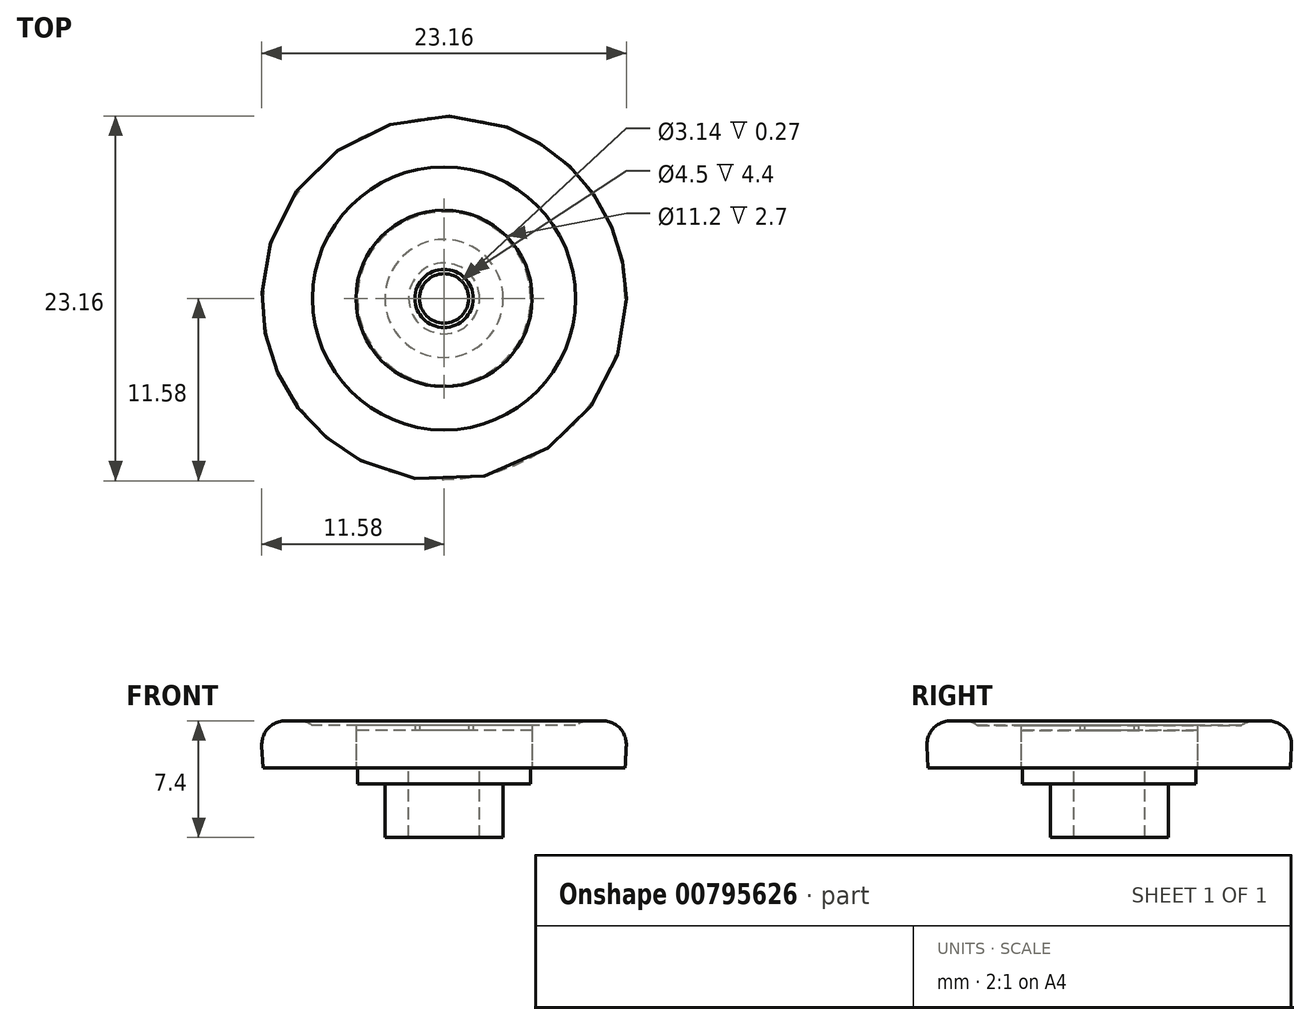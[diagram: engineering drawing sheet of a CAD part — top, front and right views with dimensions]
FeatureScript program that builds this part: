
annotation { "Feature Type Name" : "Feature", "Feature Type Description" : "" }
export const myFeature = defineFeature(function(context is Context, id is Id, definition is map)
    precondition{}
    {
        {
            var Q0;
            Q0=qCreatedBy(makeId("Top.planeOp"),FACE);
            var sketch = newSketch(context, id + "F0", { "sketchPlane" : qUnion([Q0])});
            skCircle(sketch, "E0", {"center": v(0, 0) * mm, "radius": 11.5 * mm});
            skCircle(sketch, "E1", {"center": v(0, 0) * mm, "radius": 8.5 * mm});
            skCircle(sketch, "E2", {"center": v(0, 0) * mm, "radius": 5.6 * mm});
            skSolve(sketch);
        }
        {
            var Q0;
            Q0 = qSketchRegion(id + "F0", true);
            extrude(context, id + "F1", {"entities" : qUnion([Q0]), "depth" : 3 * mm, "offsetDistance" : 25 * mm, "hasDraft" : true, "draftAngle" : 3 * degree});
        }
        {
            var Q0;
            Q0=makeQuery(id+"F0.imprint","IMPRINT",FACE,{"disambiguationData":[TD([[makeQuery(id+"F0.imprint","IMPRINT",EDGE,{"derivedFrom":sQuery(id+"F0.wireOp",EDGE,"E1")}),1.0]])]});
            extrude(context, id + "F2", {"entities" : qUnion([Q0]), "operationType" : NewBodyOperationType.ADD, "depth" : 2.7 * mm, "offsetDistance" : 25 * mm});
        }
        {
            var Q0;
            Q0=makeQuery(id+"F0.imprint","IMPRINT",FACE,{"disambiguationData":[TD([[makeQuery(id+"F0.imprint","IMPRINT",EDGE,{"derivedFrom":sQuery(id+"F0.wireOp",EDGE,"sJWBEL4Q-zqKP-wKAH-Xvia-YZl9IQGTlxIB")}),1.0]])]});
            var Q1;
            Q1=makeQuery(id+"F0.imprint","IMPRINT",FACE,{"disambiguationData":[TD([[makeQuery(id+"F0.imprint","IMPRINT",EDGE,{"derivedFrom":sQuery(id+"F0.wireOp",EDGE,"W3Ua214L-QGfU-jLto-IY45-T6SqmYm5Pf0N")}),1.0]])]});
            var Q2;
            Q2=makeQuery(id+"F0.imprint","IMPRINT",FACE,{"disambiguationData":[TD([[makeQuery(id+"F0.imprint","IMPRINT",EDGE,{"derivedFrom":sQuery(id+"F0.wireOp",EDGE,"KE1PqsyT-DHGX-8diU-NURI-yFHnlOPL5x9j")}),1.0]])]});
            var Q3;
            Q3=makeQuery(id+"F0.imprint","IMPRINT",FACE,{"disambiguationData":[TD([[makeQuery(id+"F0.imprint","IMPRINT",EDGE,{"derivedFrom":sQuery(id+"F0.wireOp",EDGE,"93cc1e78-3582-4651-860f-33596dd8aeea")}),1.0]])]});
            var Q4;
            Q4=makeQuery(id+"F0.imprint","IMPRINT",FACE,{"disambiguationData":[TD([[makeQuery(id+"F0.imprint","IMPRINT",EDGE,{"derivedFrom":sQuery(id+"F0.wireOp",EDGE,"580936a7-a73b-495c-908d-01e9c6adc14b")}),1.0]])]});
            var Q5;
            Q5=makeQuery(id+"F0.imprint","IMPRINT",FACE,{"disambiguationData":[TD([[makeQuery(id+"F0.imprint","IMPRINT",EDGE,{"derivedFrom":sQuery(id+"F0.wireOp",EDGE,"914aee80-40cc-4c9e-a0ba-7517bd072fba")}),1.0]])]});
            var Q6;
            Q6=makeQuery(id+"F0.imprint","IMPRINT",FACE,{"disambiguationData":[TD([[makeQuery(id+"F0.imprint","IMPRINT",EDGE,{"derivedFrom":sQuery(id+"F0.wireOp",EDGE,"tJGHLqfq-XDhS-PHHt-wrfx-KiIFVS5NVcas")}),1.0]])]});
            var Q7;
            Q7=makeQuery(id+"F0.imprint","IMPRINT",FACE,{"disambiguationData":[TD([[makeQuery(id+"F0.imprint","IMPRINT",EDGE,{"derivedFrom":sQuery(id+"F0.wireOp",EDGE,"QfYnkFk0-Tl5y-BypX-IXop-PRvAgd9sKDpf")}),1.0]])]});
            var Q8;
            Q8=makeQuery(id+"F0.imprint","IMPRINT",FACE,{"disambiguationData":[TD([[makeQuery(id+"F0.imprint","IMPRINT",EDGE,{"derivedFrom":sQuery(id+"F0.wireOp",EDGE,"Y070iHcx-JKvN-373v-bcgJ-Ptq9Z7jqXRuu")}),1.0]])]});
            var Q9;
            {var subQ0=sQuery(id+"F0.wireOp",EDGE,"364aceb5-e4ae-42a2-838b-8d2f1a538a20");var subQ5=sQuery(id+"F0.wireOp",EDGE,"E2");var subQ8=makeQuery(id+"F0.imprint","INTERSECT",VERTEX,{"disambiguationData":[OD(0.0)],"derivedFrom":[subQ5,subQ0]});Q9=makeQuery(id+"F0.imprint","IMPRINT",FACE,{"disambiguationData":[TD([[makeQuery(id+"F0.imprint","IMPRINT",EDGE,{"disambiguationData":[TD([[subQ8,1.0]])],"derivedFrom":subQ5}),1.0]])]});}
            var Q10;
            {var subQ1=sQuery(id+"F0.wireOp",EDGE,"E2");var subQ3=sQuery(id+"F0.wireOp",EDGE,"240fa6d0-75f4-4649-a5dc-fb8ea6b493ce");var subQ4=makeQuery(id+"F0.imprint","INTERSECT",VERTEX,{"disambiguationData":[OD(0.0)],"derivedFrom":[subQ1,subQ3]});Q10=makeQuery(id+"F0.imprint","IMPRINT",FACE,{"disambiguationData":[TD([[makeQuery(id+"F0.imprint","IMPRINT",EDGE,{"disambiguationData":[TD([[subQ4,-1.0]])],"derivedFrom":subQ1}),1.0]])]});}
            var Q11;
            {var subQ0=sQuery(id+"F0.wireOp",EDGE,"a4363b79-0781-4621-b503-21fbbac03dd4");Q11=makeQuery(id+"F0.imprint","IMPRINT",FACE,{"disambiguationData":[TD([[makeQuery(id+"F0.imprint","IMPRINT",EDGE,{"derivedFrom":subQ0}),1.0]])]});}
            var Q12;
            Q12=makeQuery(id+"F0.imprint","IMPRINT",FACE,{"disambiguationData":[TD([[makeQuery(id+"F0.imprint","IMPRINT",EDGE,{"derivedFrom":sQuery(id+"F0.wireOp",EDGE,"dakPGjOR-qgw5-qXTv-UFbR-eR2Q9f3JjfMY")}),1.0]])]});
            var Q13;
            Q13=makeQuery(id+"F0.imprint","IMPRINT",FACE,{"disambiguationData":[TD([[makeQuery(id+"F0.imprint","IMPRINT",EDGE,{"derivedFrom":sQuery(id+"F0.wireOp",EDGE,"c86a8116-1d08-438b-9353-779b471d0a26")}),-1.0]])]});
            var Q14;
            {var subQ5=sQuery(id+"F0.wireOp",EDGE,"240fa6d0-75f4-4649-a5dc-fb8ea6b493ce");Q14=makeQuery(id+"F0.imprint","IMPRINT",FACE,{"disambiguationData":[TD([[makeQuery(id+"F0.imprint","IMPRINT",EDGE,{"derivedFrom":subQ5}),-1.0]])]});}
            var Q15;
            {var subQ0=sQuery(id+"F0.wireOp",EDGE,"cf34df1f-d6ec-4883-8101-f005d7a4a38d");Q15=makeQuery(id+"F0.imprint","IMPRINT",FACE,{"disambiguationData":[TD([[makeQuery(id+"F0.imprint","IMPRINT",EDGE,{"derivedFrom":subQ0}),-1.0]])]});}
            extrude(context, id + "F3", {"entities" : qUnion([Q0, Q1, Q2, Q3, Q4, Q5, Q6, Q7, Q8, Q9, Q10, Q11, Q12, Q13, Q14, Q15]), "depth" : 2.4 * mm, "offsetDistance" : 25 * mm});
        }
        {
            var Q0;
            Q0=makeQuery(id+"F1.opExtrude","CAP_EDGE",EDGE,{"disambiguationData":[OSD([sQuery(id+"F0.wireOp",EDGE,"E0")])],"isStart":false});
            var Q1;
            Q1=makeQuery(id+"F1.opExtrude","CAP_EDGE",EDGE,{"disambiguationData":[OSD([sQuery(id+"F0.wireOp",EDGE,"E1")])],"isStart":false});
            fillet(context, id + "F4", {"entities" : qUnion([Q0, Q1]), "radius" : 1.5 * mm, "tangentPropagation" : true, "allowEdgeOverflow" : false});
        }
        {
            var Q0;
            Q0=qCreatedBy(makeId("Top.planeOp"),FACE);
            var sketch = newSketch(context, id + "F5", { "sketchPlane" : qUnion([Q0])});
            skCircle(sketch, "E3", {"center": v(0, 0) * mm, "radius": 5.5 * mm});
            skCircle(sketch, "E4", {"center": v(0, 0) * mm, "radius": 3.75 * mm});
            skCircle(sketch, "E5", {"center": v(0, 0) * mm, "radius": 2.25 * mm});
            skSolve(sketch);
        }
        {
            var Q0;
            Q0 = qSketchRegion(id + "F5", true);
            extrude(context, id + "F6", {"entities" : qUnion([Q0]), "operationType" : NewBodyOperationType.ADD, "oppositeDirection" : true, "depth" : 1 * mm, "offsetDistance" : 25 * mm});
        }
        {
            var Q0;
            Q0=makeQuery(id+"F5.imprint","IMPRINT",FACE,{"disambiguationData":[TD([[makeQuery(id+"F5.imprint","IMPRINT",EDGE,{"derivedFrom":sQuery(id+"F5.wireOp",EDGE,"E4")}),1.0]])]});
            extrude(context, id + "F7", {"entities" : qUnion([Q0]), "operationType" : NewBodyOperationType.ADD, "oppositeDirection" : true, "depth" : 4.4 * mm, "offsetDistance" : 25 * mm});
        }
        {
            var Q0;
            Q0=qCreatedBy(makeId("Top.planeOp"),FACE);
            cPlane(context, id + "F8", {"entities" : qUnion([Q0]), "cplaneType" : CPlaneType.OFFSET, "offset" : 2.4 * mm, "width" : 150 * mm, "height" : 150 * mm});
        }
        {
            var Q0;
            Q0=qCreatedBy(id+"F8.planeOp",FACE);
            var sketch = newSketch(context, id + "F9", { "sketchPlane" : qUnion([Q0])});
            skCircle(sketch, "E6", {"center": v(0, 0) * mm, "radius": 1.85 * mm});
            skCircle(sketch, "E7", {"center": v(0, 0) * mm, "radius": 1.57 * mm});
            skCircle(sketch, "E8", {"center": v(0, 0) * mm, "radius": 5.6 * mm});
            skFitSpline(sketch, "E9", {"points": [v(1.78, -0.5) * mm, v(1.79, -0.56) * mm, v(1.81, -0.61) * mm, v(1.9, -0.7) * mm, v(2.12, -0.88) * mm, v(2.47, -1.1) * mm, v(2.86, -1.37) * mm, v(3.48, -1.75) * mm, v(4.06, -2.14) * mm, v(4.51, -2.4) * mm, v(4.63, -2.44) * mm, v(4.76, -2.46) * mm, v(4.87, -2.44) * mm, v(4.98, -2.4) * mm, v(5.1, -2.3) * mm], "startDerivative": vector(-0.8, -2.81) * mm, "endDerivative": vector(1.02, 2.24) * mm});
            skFitSpline(sketch, "E10", {"points": [v(-1.07, -1.51) * mm, v(-1.2, -1.46) * mm, v(-1.28, -1.46) * mm, v(-1.4, -1.48) * mm, v(-1.66, -1.6) * mm, v(-2.02, -1.8) * mm, v(-2.43, -2.03) * mm, v(-3.06, -2.4) * mm, v(-3.68, -2.73) * mm, v(-4.11, -3) * mm, v(-4.22, -3.08) * mm, v(-4.3, -3.18) * mm, v(-4.36, -3.3) * mm, v(-4.37, -3.42) * mm, v(-4.3, -3.58) * mm], "startDerivative": vector(-2.5, 1.82) * mm, "endDerivative": vector(2.87, -3.5) * mm});
            skFitSpline(sketch, "E11", {"points": [v(0.97, -1.57) * mm, v(1.06, -1.54) * mm, v(1.16, -1.52) * mm, v(1.3, -1.5) * mm, v(1.46, -1.55) * mm, v(1.84, -1.76) * mm, v(2.37, -2.05) * mm, v(2.81, -2.3) * mm, v(3.45, -2.66) * mm, v(4, -2.98) * mm, v(4.14, -3.06) * mm, v(4.24, -3.15) * mm, v(4.3, -3.27) * mm, v(4.33, -3.38) * mm, v(4.31, -3.53) * mm, v(4.25, -3.64) * mm, v(4.25, -3.64) * mm], "startDerivative": vector(2.43, 1.54) * mm, "endDerivative": vector(0.65, 0.76) * mm});
            skCircle(sketch, "E12", {"center": v(2.1, -1.4) * mm, "radius": 0.22 * mm});
            skCircle(sketch, "E13", {"center": v(3.06, -1.98) * mm, "radius": 0.18 * mm});
            skCircle(sketch, "E14", {"center": v(3.83, -2.46) * mm, "radius": 0.14 * mm});
            skLineSegment(sketch, "E15", {"start": v(1.53, -1.04) * mm, "end": v(4.73, -3) * mm, "construction": true});
            skFitSpline(sketch, "E16", {"points": [v(-1.83, -0.27) * mm, v(-1.83, -0.48) * mm, v(-1.86, -0.55) * mm, v(-1.93, -0.65) * mm, v(-2.05, -0.77) * mm, v(-2.4, -1.03) * mm, v(-2.9, -1.37) * mm, v(-3.39, -1.67) * mm, v(-3.91, -2) * mm, v(-4.36, -2.26) * mm, v(-4.67, -2.42) * mm, v(-4.86, -2.46) * mm, v(-5, -2.43) * mm, v(-5.25, -1.96) * mm], "startDerivative": vector(1.36, -7.17) * mm, "endDerivative": vector(-3.92, 9.14) * mm});
            skCircle(sketch, "E17", {"center": v(-2.18, -1.4) * mm, "radius": 0.22 * mm});
            skCircle(sketch, "E18", {"center": v(-3.14, -1.99) * mm, "radius": 0.18 * mm});
            skCircle(sketch, "E19", {"center": v(-3.91, -2.46) * mm, "radius": 0.14 * mm});
            skLineSegment(sketch, "E20", {"start": v(-1.54, -1.02) * mm, "end": v(-4.76, -2.95) * mm, "construction": true});
            skFitSpline(sketch, "E21", {"points": [v(-0.72, 1.7) * mm, v(-0.59, 1.81) * mm, v(-0.52, 1.91) * mm, v(-0.47, 2.08) * mm, v(-0.46, 2.3) * mm, v(-0.45, 2.72) * mm, v(-0.44, 3.2) * mm, v(-0.44, 3.91) * mm, v(-0.42, 4.62) * mm, v(-0.44, 5.13) * mm, v(-0.47, 5.26) * mm, v(-0.51, 5.38) * mm, v(-0.59, 5.46) * mm, v(-0.7, 5.53) * mm, v(-0.82, 5.54) * mm], "startDerivative": vector(2.8, 0.8) * mm, "endDerivative": vector(-2.44, -0.32) * mm});
            skFitSpline(sketch, "E22", {"points": [v(0.74, 1.7) * mm, v(0.67, 1.75) * mm, v(0.6, 1.83) * mm, v(0.51, 1.94) * mm, v(0.47, 2.1) * mm, v(0.44, 2.53) * mm, v(0.43, 3.14) * mm, v(0.42, 3.65) * mm, v(0.4, 4.38) * mm, v(0.39, 5.1) * mm, v(0.4, 5.24) * mm, v(0.44, 5.37) * mm, v(0.5, 5.45) * mm, v(0.58, 5.5) * mm, v(0.67, 5.53) * mm, v(0.84, 5.54) * mm], "startDerivative": vector(-1.87, 1.36) * mm, "endDerivative": vector(4.35, -0.63) * mm});
            skCircle(sketch, "E23", {"center": v(0, 2.56) * mm, "radius": 0.22 * mm});
            skCircle(sketch, "E24", {"center": v(0, 3.73) * mm, "radius": 0.18 * mm});
            skCircle(sketch, "E25", {"center": v(0, 4.59) * mm, "radius": 0.14 * mm});
            skLineSegment(sketch, "E26", {"start": v(0, 1.85) * mm, "end": v(0, 5.6) * mm, "construction": true});
            skCircle(sketch, "E27", {"center": v(0, 0) * mm, "radius": 5.95 * mm});
            skFitSpline(sketch, "E28", {"points": [v(-1.05, -0.83) * mm, v(-1.13, -0.72) * mm, v(-1.22, -0.56) * mm, v(-1.28, -0.37) * mm, v(-1.3, -0.17) * mm, v(-1.32, 0.02) * mm, v(-1.3, 0.2) * mm, v(-1.22, 0.43) * mm, v(-1.13, 0.6) * mm, v(-1, 0.78) * mm, v(-0.85, 0.93) * mm, v(-0.72, 1.04) * mm, v(-0.56, 1.13) * mm, v(-0.45, 1.18) * mm, v(-0.45, 1.18) * mm], "startDerivative": vector(-1.28, 1.58) * mm, "endDerivative": vector(-0.6, -0.06) * mm});
            skFitSpline(sketch, "E29", {"points": [v(-0.64, 0.92) * mm, v(-0.75, 0.85) * mm, v(-0.84, 0.76) * mm, v(-0.93, 0.66) * mm, v(-1.01, 0.53) * mm, v(-1.08, 0.36) * mm, v(-1.1, 0.21) * mm, v(-1.12, 0.05) * mm, v(-1.12, -0.13) * mm], "startDerivative": vector(-1.01, -0.52) * mm, "endDerivative": vector(0, -1.33) * mm});
            skFitSpline(sketch, "E30", {"points": [v(-1.12, -0.13) * mm, v(-0.9, -0.13) * mm, v(-0.65, -0.13) * mm], "startDerivative": vector(0.46, 0) * mm, "endDerivative": vector(0.47, 0) * mm});
            skFitSpline(sketch, "E31", {"points": [v(-0.65, -0.13) * mm, v(-0.65, 0.18) * mm, v(-0.65, 0.52) * mm, v(-0.64, 0.92) * mm], "startDerivative": vector(0, 0.98) * mm, "endDerivative": vector(0.04, 1.13) * mm});
            skFitSpline(sketch, "E32", {"points": [v(-0.45, 1.18) * mm, v(-0.45, 0.64) * mm, v(-0.45, -0.19) * mm, v(-0.45, -0.76) * mm, v(-0.45, -1.2) * mm], "startDerivative": vector(0, -2.1) * mm, "endDerivative": vector(0, -2.03) * mm});
            skFitSpline(sketch, "E33", {"points": [v(-0.45, -1.2) * mm, v(-0.53, -1.16) * mm, v(-0.64, -1.11) * mm], "startDerivative": vector(-0.17, 0.1) * mm, "endDerivative": vector(-0.22, 0.1) * mm});
            skFitSpline(sketch, "E34", {"points": [v(-0.64, -1.11) * mm, v(-0.64, -0.76) * mm, v(-0.64, -0.5) * mm, v(-0.64, -0.29) * mm], "startDerivative": vector(0, 0.95) * mm, "endDerivative": vector(0, 0.7) * mm});
            skFitSpline(sketch, "E35", {"points": [v(-0.64, -0.29) * mm, v(-0.85, -0.29) * mm, v(-1.05, -0.29) * mm], "startDerivative": vector(-0.4, 0) * mm, "endDerivative": vector(-0.41, 0) * mm});
            skFitSpline(sketch, "E36", {"points": [v(-1.05, -0.29) * mm, v(-1.04, -0.4) * mm, v(-1.01, -0.5) * mm, v(-0.95, -0.6) * mm, v(-0.9, -0.68) * mm], "startDerivative": vector(0.02, -0.66) * mm, "endDerivative": vector(0.26, -0.3) * mm});
            skFitSpline(sketch, "E37", {"points": [v(-0.9, -0.68) * mm, v(-0.97, -0.75) * mm, v(-1.05, -0.83) * mm], "startDerivative": vector(-0.17, -0.14) * mm, "endDerivative": vector(-0.15, -0.16) * mm});
            skSolve(sketch);
        }
        {
            var Q0;
            Q0=makeQuery(id+"F9.imprint","IMPRINT",FACE,{"disambiguationData":[TD([[makeQuery(id+"F9.imprint","IMPRINT",EDGE,{"derivedFrom":sQuery(id+"F9.wireOp",EDGE,"E7")}),-1.0]])]});
            var Q1;
            {var subQ0=sQuery(id+"F9.wireOp",EDGE,"E9");Q1=makeQuery(id+"F9.imprint","IMPRINT",FACE,{"disambiguationData":[TD([[makeQuery(id+"F9.imprint","IMPRINT",EDGE,{"derivedFrom":subQ0}),-1.0]])]});}
            var Q2;
            {var subQ0=sQuery(id+"F9.wireOp",EDGE,"E22");Q2=makeQuery(id+"F9.imprint","IMPRINT",FACE,{"disambiguationData":[TD([[makeQuery(id+"F9.imprint","IMPRINT",EDGE,{"derivedFrom":subQ0}),1.0]])]});}
            var Q3;
            {var subQ5=sQuery(id+"F9.wireOp",EDGE,"E10");Q3=makeQuery(id+"F9.imprint","IMPRINT",FACE,{"disambiguationData":[TD([[makeQuery(id+"F9.imprint","IMPRINT",EDGE,{"derivedFrom":subQ5}),-1.0]])]});}
            extrude(context, id + "F10", {"entities" : qUnion([Q0, Q1, Q2, Q3]), "depth" : 0.3 * mm, "offsetDistance" : 25 * mm});
        }
        {
            var Q0;
            Q0=makeQuery(id+"F10.opExtrude","CAP_EDGE",EDGE,{"disambiguationData":[OSD([sQuery(id+"F9.wireOp",EDGE,"E10")])],"isStart":false});
            var Q1;
            Q1=makeQuery(id+"F10.opExtrude","CAP_EDGE",EDGE,{"disambiguationData":[OSD([sQuery(id+"F9.wireOp",EDGE,"E9")])],"isStart":false});
            var Q2;
            {var subQ0=sQuery(id+"F9.wireOp",EDGE,"E6");Q2=makeQuery(id+"F10.opExtrude","CAP_EDGE",EDGE,{"disambiguationData":[OSD([subQ0]),TDD([makeQuery(id+"F9.imprint","IMPRINT",EDGE,{"disambiguationData":[TD([[makeQuery(id+"F9.imprint","INTERSECT",VERTEX,{"derivedFrom":[subQ0,sQuery(id+"F9.wireOp",EDGE,"E9")]}),-1.0]])],"derivedFrom":subQ0})])],"isStart":false});}
            var Q3;
            Q3=makeQuery(id+"F10.opExtrude","CAP_EDGE",EDGE,{"disambiguationData":[OSD([sQuery(id+"F9.wireOp",EDGE,"E22")])],"isStart":false});
            var Q4;
            Q4=makeQuery(id+"F10.opExtrude","CAP_EDGE",EDGE,{"disambiguationData":[OSD([sQuery(id+"F9.wireOp",EDGE,"E21")])],"isStart":false});
            var Q5;
            {var subQ0=sQuery(id+"F9.wireOp",EDGE,"E6");Q5=makeQuery(id+"F10.opExtrude","CAP_EDGE",EDGE,{"disambiguationData":[OSD([subQ0]),TDD([makeQuery(id+"F9.imprint","IMPRINT",EDGE,{"disambiguationData":[TD([[makeQuery(id+"F9.imprint","INTERSECT",VERTEX,{"disambiguationData":[OD(0.0)],"derivedFrom":[subQ0,sQuery(id+"F9.wireOp",EDGE,"E16")]}),1.0]])],"derivedFrom":subQ0})])],"isStart":false});}
            var Q6;
            Q6=makeQuery(id+"F10.opExtrude","CAP_EDGE",EDGE,{"disambiguationData":[OSD([sQuery(id+"F9.wireOp",EDGE,"E16")])],"isStart":false});
            var Q7;
            Q7=makeQuery(id+"F10.opExtrude","CAP_EDGE",EDGE,{"disambiguationData":[OSD([sQuery(id+"F9.wireOp",EDGE,"E11")])],"isStart":false});
            var Q8;
            {var subQ0=sQuery(id+"F9.wireOp",EDGE,"E6");var subQ1=makeQuery(id+"F9.imprint","IMPRINT",VERTEX,{"disambiguationData":[OD(1.0)],"derivedFrom":subQ0});var subQ2=makeQuery(id+"F9.imprint","IMPRINT",VERTEX,{"disambiguationData":[OD(0.0)],"derivedFrom":subQ0});Q8=makeQuery(id+"F10.opExtrude","CAP_EDGE",EDGE,{"disambiguationData":[OSD([subQ0]),TDD([makeQuery(id+"F9.imprint","IMPRINT",EDGE,{"disambiguationData":[TD([[subQ2,1.0]])],"derivedFrom":subQ0}),makeQuery(id+"F9.imprint","IMPRINT",EDGE,{"disambiguationData":[TD([[subQ2,-1.0]])],"derivedFrom":subQ0}),makeQuery(id+"F9.imprint","IMPRINT",EDGE,{"disambiguationData":[TD([[subQ1,-1.0]])],"derivedFrom":subQ0})])],"isStart":false});}
            var Q9;
            Q9=makeQuery(id+"F10.opExtrude","CAP_EDGE",EDGE,{"disambiguationData":[OSD([sQuery(id+"F9.wireOp",EDGE,"E7")])],"isStart":false});
            fillet(context, id + "F11", {"entities" : qUnion([Q0, Q1, Q2, Q3, Q4, Q5, Q6, Q7, Q8, Q9]), "radius" : 0.03 * mm, "tangentPropagation" : true, "allowEdgeOverflow" : false});
        }
    });
